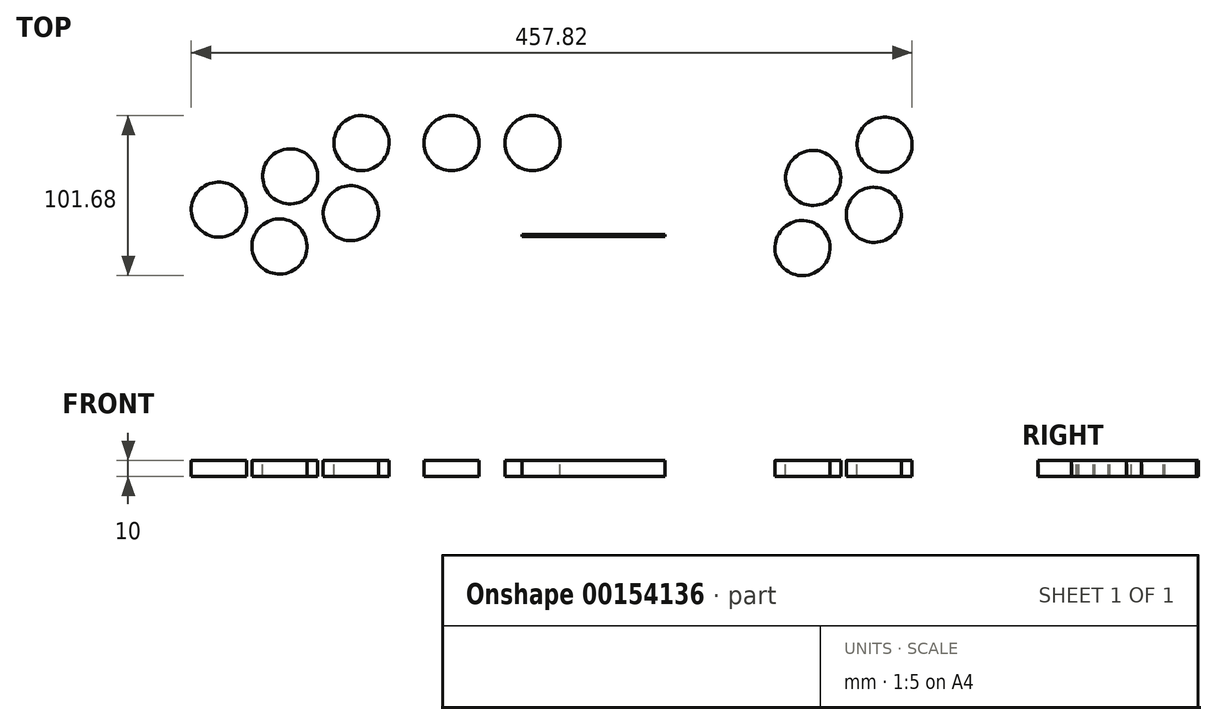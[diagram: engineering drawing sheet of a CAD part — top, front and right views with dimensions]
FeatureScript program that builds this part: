
annotation { "Feature Type Name" : "Feature", "Feature Type Description" : "" }
export const myFeature = defineFeature(function(context is Context, id is Id, definition is map)
    precondition{}
    {
        {
            var Q0;
            Q0=qCreatedBy(makeId("Top.planeOp"),FACE);
            var sketch = newSketch(context, id + "F0", { "sketchPlane" : qUnion([Q0])});
            skLineSegment(sketch, "E0.bottom", {"start": v(325, -100) * mm, "end": v(-325, -100) * mm});
            skLineSegment(sketch, "E0.top", {"start": v(325, 100) * mm, "end": v(-325, 100) * mm});
            skLineSegment(sketch, "E0.left", {"start": v(325, -100) * mm, "end": v(325, 100) * mm});
            skLineSegment(sketch, "E0.right", {"start": v(-325, -100) * mm, "end": v(-325, 100) * mm});
            skPoint(sketch, "E0.middle", {"position": v(0, 0) * mm});
            skSolve(sketch);
        }
        {
            var Q0;
            Q0 = qSketchRegion(id + "F0", true);
            extrude(context, id + "F1", {"entities" : qUnion([Q0]), "depth" : 10 * mm});
        }
        {
            var Q0;
            Q0=makeQuery(id+"F1.opExtrude","SWEPT_FACE",FACE,{"disambiguationData":[OSD([sQuery(id+"F0.wireOp",EDGE,"E0.left")])]});
            var sketch = newSketch(context, id + "F2", { "sketchPlane" : qUnion([Q0])});
            skLineSegment(sketch, "E1.bottom", {"start": v(-100, 0) * mm, "end": v(100, 0) * mm});
            skLineSegment(sketch, "E1.top", {"start": v(-100, 10) * mm, "end": v(100, 10) * mm});
            skLineSegment(sketch, "E1.left", {"start": v(-100, 0) * mm, "end": v(-100, 10) * mm});
            skLineSegment(sketch, "E1.right", {"start": v(100, 0) * mm, "end": v(100, 10) * mm});
            skPoint(sketch, "E2", {"position": v(-90, 5) * mm});
            skPoint(sketch, "E3", {"position": v(90, 5) * mm});
            skSolve(sketch);
        }
        {
            var Q0;
            Q0=makeQuery(id+"F1.opExtrude","SWEPT_FACE",FACE,{"disambiguationData":[OSD([sQuery(id+"F0.wireOp",EDGE,"E0.right")])]});
            var sketch = newSketch(context, id + "F3", { "sketchPlane" : qUnion([Q0])});
            skLineSegment(sketch, "E4.bottom", {"start": v(-100, 0) * mm, "end": v(100, 0) * mm});
            skLineSegment(sketch, "E4.top", {"start": v(-100, 10) * mm, "end": v(100, 10) * mm});
            skLineSegment(sketch, "E4.left", {"start": v(-100, 0) * mm, "end": v(-100, 10) * mm});
            skLineSegment(sketch, "E4.right", {"start": v(100, 0) * mm, "end": v(100, 10) * mm});
            skPoint(sketch, "E5", {"position": v(-90, 5) * mm});
            skPoint(sketch, "E6", {"position": v(90, 5) * mm});
            skSolve(sketch);
        }
        {
            var Q0;
            Q0=sQuery(id+"F2.wireOp",VERTEX,"E3");
            var Q1;
            Q1=sQuery(id+"F2.wireOp",VERTEX,"E2");
            var Q2;
            Q2=sQuery(id+"F3.wireOp",VERTEX,"E6");
            var Q3;
            Q3=sQuery(id+"F3.wireOp",VERTEX,"E5");
            var Q4;
            Q4=makeQuery(id+"F1.opExtrude","SWEPT_BODY",BODY,{"disambiguationData":[OSD([sQuery(id+"F0.wireOp",EDGE,"E0.bottom"),sQuery(id+"F0.wireOp",EDGE,"E0.top"),sQuery(id+"F0.wireOp",EDGE,"E0.left"),sQuery(id+"F0.wireOp",EDGE,"E0.right")])]});
            hole(context, id + "F4", {"style" : HoleStyle.SIMPLE, "endStyle" : HoleEndStyle.BLIND, "standardTappedOrClearance" : lookupTablePath({ "standard" : "ISO", "engagement" : "75%", "pitch" : "1 mm", "size" : "M6", "type" : "Tapped" }), "standardBlindInLast" : lookupTablePath({ "standard" : "ISO", "engagement" : "75%", "pitch" : "1 mm", "size" : "M6", "type" : "Tapped" }), "holeDiameter" : 5 * mm, "holeDepth" : 20 * mm, "locations" : qUnion([Q0, Q1, Q2, Q3]), "scope" : qUnion([Q4]), "majorDiameter" : 6 * mm});
        }
        {
            var Q0;
            Q0=makeQuery(id+"F1.opExtrude","CAP_FACE",FACE,{"disambiguationData":[OSD([sQuery(id+"F0.wireOp",EDGE,"E0.bottom"),sQuery(id+"F0.wireOp",EDGE,"E0.top"),sQuery(id+"F0.wireOp",EDGE,"E0.left"),sQuery(id+"F0.wireOp",EDGE,"E0.right")])],"isStart":false});
            var sketch = newSketch(context, id + "F5", { "sketchPlane" : qUnion([Q0])});
            skLineSegment(sketch, "E7", {"start": v(-325, -100) * mm, "end": v(325, -100) * mm});
            skLineSegment(sketch, "E8", {"start": v(325, -100) * mm, "end": v(325, 100) * mm});
            skLineSegment(sketch, "E9", {"start": v(325, 100) * mm, "end": v(-325, 100) * mm});
            skLineSegment(sketch, "E10", {"start": v(-325, 100) * mm, "end": v(-325, -100) * mm});
            skArc(sketch, "E11", {"start": v(-176.18, 18.53) * mm, "mid": v(-167.71, 41.78) * mm, "end": v(-144.46, 33.32) * mm});
            skArc(sketch, "E12", {"start": v(-144.46, 33.32) * mm, "mid": v(-152.92, 10.06) * mm, "end": v(-176.18, 18.53) * mm});
            skArc(sketch, "E13", {"start": v(-130.86, 39.66) * mm, "mid": v(-122.4, 62.91) * mm, "end": v(-99.14, 54.45) * mm});
            skArc(sketch, "E14", {"start": v(-99.14, 54.45) * mm, "mid": v(-107.6, 31.2) * mm, "end": v(-130.86, 39.66) * mm});
            skArc(sketch, "E15", {"start": v(-92.35, 16.24) * mm, "mid": v(-83.89, 39.5) * mm, "end": v(-60.63, 31.03) * mm});
            skArc(sketch, "E16", {"start": v(-60.63, 31.03) * mm, "mid": v(-69.1, 7.77) * mm, "end": v(-92.35, 16.24) * mm});
            skArc(sketch, "E17", {"start": v(-137.67, -4.9) * mm, "mid": v(-129.2, 18.36) * mm, "end": v(-105.95, 9.9) * mm});
            skArc(sketch, "E18", {"start": v(-105.95, 9.9) * mm, "mid": v(-114.41, -13.36) * mm, "end": v(-137.67, -4.9) * mm});
            skArc(sketch, "E19", {"start": v(-85.54, 60.79) * mm, "mid": v(-77.08, 84.04) * mm, "end": v(-53.82, 75.58) * mm});
            skArc(sketch, "E20", {"start": v(-53.82, 75.58) * mm, "mid": v(-62.29, 52.32) * mm, "end": v(-85.54, 60.79) * mm});
            skLineSegment(sketch, "E21", {"start": v(-300, -70) * mm, "end": v(-209, -70) * mm});
            skLineSegment(sketch, "E22", {"start": v(-209, -70) * mm, "end": v(-209, 10) * mm});
            skLineSegment(sketch, "E23", {"start": v(-209, 10) * mm, "end": v(-300, 10) * mm});
            skLineSegment(sketch, "E24", {"start": v(-300, 10) * mm, "end": v(-300, -70) * mm});
            skArc(sketch, "E25", {"start": v(156, 18.53) * mm, "mid": v(164.47, 41.78) * mm, "end": v(187.73, 33.32) * mm});
            skArc(sketch, "E26", {"start": v(187.73, 32.32) * mm, "mid": v(179.27, 9.06) * mm, "end": v(156, 17.53) * mm});
            skArc(sketch, "E27", {"start": v(201.32, 38.66) * mm, "mid": v(209.79, 61.91) * mm, "end": v(233.04, 53.45) * mm});
            skArc(sketch, "E28", {"start": v(233.04, 53.45) * mm, "mid": v(224.58, 30.2) * mm, "end": v(201.32, 38.66) * mm});
            skArc(sketch, "E29", {"start": v(239.83, 15.24) * mm, "mid": v(248.3, 38.5) * mm, "end": v(271.55, 30.03) * mm});
            skArc(sketch, "E30", {"start": v(271.55, 30.03) * mm, "mid": v(263.09, 6.77) * mm, "end": v(239.83, 15.24) * mm});
            skArc(sketch, "E31", {"start": v(194.51, -5.9) * mm, "mid": v(202.98, 17.36) * mm, "end": v(226.24, 8.9) * mm});
            skArc(sketch, "E32", {"start": v(226.24, 8.9) * mm, "mid": v(217.77, -14.36) * mm, "end": v(194.51, -5.9) * mm});
            skArc(sketch, "E33", {"start": v(246.64, 59.79) * mm, "mid": v(255.1, 83.04) * mm, "end": v(278.36, 74.58) * mm});
            skArc(sketch, "E34", {"start": v(278.36, 74.58) * mm, "mid": v(269.9, 51.32) * mm, "end": v(246.64, 59.79) * mm});
            skLineSegment(sketch, "E35", {"start": v(32.18, -71) * mm, "end": v(123.18, -71) * mm});
            skLineSegment(sketch, "E36", {"start": v(123.18, -70) * mm, "end": v(123.18, 10) * mm});
            skLineSegment(sketch, "E37", {"start": v(123.18, 9) * mm, "end": v(32.18, 9) * mm});
            skLineSegment(sketch, "E38", {"start": v(32.18, 10) * mm, "end": v(32.18, -70) * mm});
            skArc(sketch, "E39", {"start": v(-30, 68.18) * mm, "mid": v(-12.5, 85.68) * mm, "end": v(5, 68.18) * mm});
            skArc(sketch, "E40", {"start": v(5, 68.18) * mm, "mid": v(-12.5, 50.68) * mm, "end": v(-30, 68.18) * mm});
            skArc(sketch, "E41", {"start": v(21.43, 68.18) * mm, "mid": v(38.93, 85.68) * mm, "end": v(56.43, 68.18) * mm});
            skArc(sketch, "E42", {"start": v(56.43, 68.18) * mm, "mid": v(38.93, 50.68) * mm, "end": v(21.43, 68.18) * mm});
            skCircle(sketch, "E43", {"center": v(171.87, 24.92) * mm, "radius": 17.5 * mm});
            skLineSegment(sketch, "E44.bottom", {"start": v(32.18, 10) * mm, "end": v(123.18, 10) * mm});
            skLineSegment(sketch, "E44.left", {"start": v(32.18, 10) * mm, "end": v(32.18, -71) * mm});
            skLineSegment(sketch, "E44.right", {"start": v(123.18, 10) * mm, "end": v(123.18, -71) * mm});
            skSolve(sketch);
        }
        {
            var Q0;
            Q0=makeQuery(id+"F5.imprint","IMPRINT",FACE,{"disambiguationData":[TD([[makeQuery(id+"F5.imprint","IMPRINT",EDGE,{"derivedFrom":sQuery(id+"F5.wireOp",EDGE,"E21")}),1.0]])]});
            var Q1;
            Q1=makeQuery(id+"F5.imprint","IMPRINT",FACE,{"disambiguationData":[TD([[makeQuery(id+"F5.imprint","IMPRINT",EDGE,{"derivedFrom":sQuery(id+"F5.wireOp",EDGE,"E11")}),-1.0]])]});
            var Q2;
            Q2=makeQuery(id+"F5.imprint","IMPRINT",FACE,{"disambiguationData":[TD([[makeQuery(id+"F5.imprint","IMPRINT",EDGE,{"derivedFrom":sQuery(id+"F5.wireOp",EDGE,"E17")}),-1.0]])]});
            var Q3;
            Q3=makeQuery(id+"F5.imprint","IMPRINT",FACE,{"disambiguationData":[TD([[makeQuery(id+"F5.imprint","IMPRINT",EDGE,{"derivedFrom":sQuery(id+"F5.wireOp",EDGE,"E13")}),-1.0]])]});
            var Q4;
            Q4=makeQuery(id+"F5.imprint","IMPRINT",FACE,{"disambiguationData":[TD([[makeQuery(id+"F5.imprint","IMPRINT",EDGE,{"derivedFrom":sQuery(id+"F5.wireOp",EDGE,"E15")}),-1.0]])]});
            var Q5;
            Q5=makeQuery(id+"F5.imprint","IMPRINT",FACE,{"disambiguationData":[TD([[makeQuery(id+"F5.imprint","IMPRINT",EDGE,{"derivedFrom":sQuery(id+"F5.wireOp",EDGE,"E19")}),-1.0]])]});
            var Q6;
            Q6=makeQuery(id+"F5.imprint","IMPRINT",FACE,{"disambiguationData":[TD([[makeQuery(id+"F5.imprint","IMPRINT",EDGE,{"derivedFrom":sQuery(id+"F5.wireOp",EDGE,"E39")}),-1.0]])]});
            var Q7;
            Q7=makeQuery(id+"F5.imprint","IMPRINT",FACE,{"disambiguationData":[TD([[makeQuery(id+"F5.imprint","IMPRINT",EDGE,{"derivedFrom":sQuery(id+"F5.wireOp",EDGE,"E41")}),-1.0]])]});
            var Q8;
            Q8=makeQuery(id+"F5.imprint","IMPRINT",FACE,{"disambiguationData":[TD([[makeQuery(id+"F5.imprint","IMPRINT",EDGE,{"derivedFrom":sQuery(id+"F5.wireOp",EDGE,"E35")}),1.0]])]});
            var Q9;
            Q9=makeQuery(id+"F5.imprint","IMPRINT",FACE,{"disambiguationData":[TD([[makeQuery(id+"F5.imprint","IMPRINT",EDGE,{"derivedFrom":sQuery(id+"F5.wireOp",EDGE,"E25")}),-1.0]])]});
            var Q10;
            Q10=makeQuery(id+"F5.imprint","IMPRINT",FACE,{"disambiguationData":[TD([[makeQuery(id+"F5.imprint","IMPRINT",EDGE,{"derivedFrom":sQuery(id+"F5.wireOp",EDGE,"E31")}),-1.0]])]});
            var Q11;
            Q11=makeQuery(id+"F5.imprint","IMPRINT",FACE,{"disambiguationData":[TD([[makeQuery(id+"F5.imprint","IMPRINT",EDGE,{"derivedFrom":sQuery(id+"F5.wireOp",EDGE,"E27")}),-1.0]])]});
            var Q12;
            Q12=makeQuery(id+"F5.imprint","IMPRINT",FACE,{"disambiguationData":[TD([[makeQuery(id+"F5.imprint","IMPRINT",EDGE,{"derivedFrom":sQuery(id+"F5.wireOp",EDGE,"E29")}),-1.0]])]});
            var Q13;
            Q13=makeQuery(id+"F5.imprint","IMPRINT",FACE,{"disambiguationData":[TD([[makeQuery(id+"F5.imprint","IMPRINT",EDGE,{"derivedFrom":sQuery(id+"F5.wireOp",EDGE,"E33")}),-1.0]])]});
            var Q14;
            {var subQ0=sQuery(id+"F5.wireOp",EDGE,"E43");var subQ1=makeQuery(id+"F5.imprint","IMPRINT",VERTEX,{"disambiguationData":[OD(0.0)],"derivedFrom":subQ0});Q14=makeQuery(id+"F5.imprint","IMPRINT",FACE,{"disambiguationData":[TD([[makeQuery(id+"F5.imprint","IMPRINT",EDGE,{"disambiguationData":[TD([[subQ1,1.0]])],"derivedFrom":subQ0}),1.0]])]});}
            var Q15;
            {var subQ3=sQuery(id+"F5.wireOp",EDGE,"E37");Q15=makeQuery(id+"F5.imprint","IMPRINT",FACE,{"disambiguationData":[TD([[makeQuery(id+"F5.imprint","IMPRINT",EDGE,{"derivedFrom":subQ3}),1.0]])]});}
            extrude(context, id + "F6", {"entities" : qUnion([Q0, Q1, Q2, Q3, Q4, Q5, Q6, Q7, Q8, Q9, Q10, Q11, Q12, Q13, Q14, Q15]), "operationType" : NewBodyOperationType.REMOVE, "oppositeDirection" : true, "depth" : 25 * mm});
        }
    });
